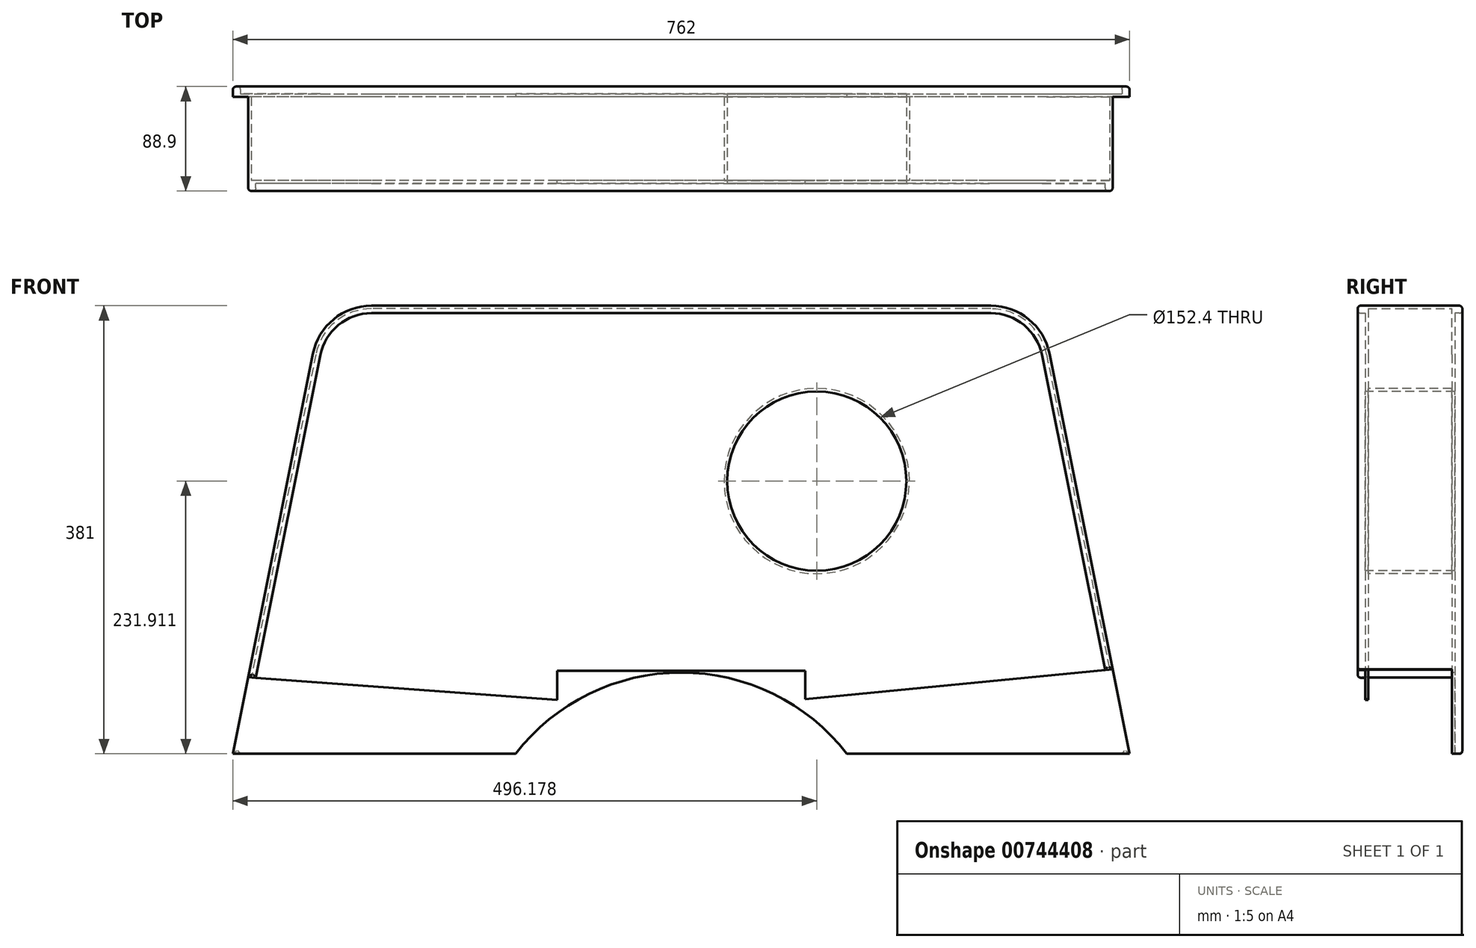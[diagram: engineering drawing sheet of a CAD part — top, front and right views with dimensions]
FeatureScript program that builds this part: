
annotation { "Feature Type Name" : "Feature", "Feature Type Description" : "" }
export const myFeature = defineFeature(function(context is Context, id is Id, definition is map)
    precondition{}
    {
        {
            var Q0;
            Q0=qCreatedBy(makeId("Top.planeOp"),FACE);
            var sketch = newSketch(context, id + "F0", { "sketchPlane" : qUnion([Q0])});
            skLineSegment(sketch, "E0.bottom", {"start": v(381, -38.1) * mm, "end": v(-381, -38.1) * mm});
            skLineSegment(sketch, "E0.top", {"start": v(381, 38.1) * mm, "end": v(-381, 38.1) * mm});
            skLineSegment(sketch, "E0.left", {"start": v(381, -38.1) * mm, "end": v(381, 38.1) * mm});
            skLineSegment(sketch, "E0.right", {"start": v(-381, -38.1) * mm, "end": v(-381, 38.1) * mm});
            skPoint(sketch, "E0.middle", {"position": v(0, 0) * mm});
            skSolve(sketch);
        }
        {
            var Q0;
            Q0=qSketchRegion(id+"F0",true);
            extrude(context, id + "F1", {"entities" : qUnion([Q0]), "depth" : 609.6 * mm});
        }
        {
            var Q0;
            Q0=makeQuery(id+"F1.opExtrude","SWEPT_FACE",FACE,{"disambiguationData":[OSD([sQuery(id+"F0.wireOp",EDGE,"E0.bottom")])]});
            var sketch = newSketch(context, id + "F2", { "sketchPlane" : qUnion([Q0])});
            skLineSegment(sketch, "E1", {"start": v(0, 381) * mm, "end": v(-304.8, 381) * mm});
            skLineSegment(sketch, "E2", {"start": v(-304.8, 381) * mm, "end": v(-381, 0) * mm});
            skLineSegment(sketch, "E3", {"start": v(0, 381) * mm, "end": v(304.8, 381) * mm});
            skLineSegment(sketch, "E4", {"start": v(304.8, 381) * mm, "end": v(381, 0) * mm});
            skPoint(sketch, "E5.center.orphan", {"position": v(0, 0) * mm});
            skSolve(sketch);
        }
        {
            var Q0;
            {var subQ1=sQuery(id+"F0.wireOp",EDGE,"E0.bottom");Q0=makeQuery(id+"F2.imprint","IMPRINT",FACE,{"disambiguationData":[TD([[makeQuery(id+"F2.imprint","IMPRINT",EDGE,{"derivedFrom":makeQuery(id+"F1.opExtrude","CAP_EDGE",EDGE,{"disambiguationData":[OSD([subQ1])],"isStart":false})}),1.0]])]});}
            extrude(context, id + "F3", {"entities" : qUnion([Q0]), "operationType" : NewBodyOperationType.REMOVE, "endBound" : BoundingType.THROUGH_ALL, "oppositeDirection" : true, "depth" : 25.4 * mm});
        }
        {
            var Q0;
            Q0=makeQuery(id+"F1.opExtrude","SWEPT_FACE",FACE,{"disambiguationData":[OSD([sQuery(id+"F0.wireOp",EDGE,"E0.bottom")])]});
            var sketch = newSketch(context, id + "F4", { "sketchPlane" : qUnion([Q0])});
            skCircle(sketch, "E6", {"center": v(115.18, 231.91) * mm, "radius": 76.2 * mm});
            skSolve(sketch);
        }
        {
            var Q0;
            Q0=makeQuery(id+"F4.imprint","IMPRINT",FACE,{"disambiguationData":[TD([[makeQuery(id+"F4.imprint","IMPRINT",EDGE,{"derivedFrom":sQuery(id+"F4.wireOp",EDGE,"E6")}),1.0]])]});
            extrude(context, id + "F5", {"entities" : qUnion([Q0]), "operationType" : NewBodyOperationType.REMOVE, "endBound" : BoundingType.THROUGH_ALL, "oppositeDirection" : true, "depth" : 25.4 * mm});
        }
        {
            var Q0;
            Q0=makeQuery(id+"F1.opExtrude","CAP_FACE",FACE,{"disambiguationData":[OSD([sQuery(id+"F0.wireOp",EDGE,"E0.bottom"),sQuery(id+"F0.wireOp",EDGE,"E0.top"),sQuery(id+"F0.wireOp",EDGE,"E0.left"),sQuery(id+"F0.wireOp",EDGE,"E0.right")])],"isStart":true});
            extrude(context, id + "F6", {"entities" : qUnion([Q0]), "operationType" : NewBodyOperationType.ADD, "depth" : 203.2 * mm});
        }
        {
            var Q0;
            {var subQ0=sQuery(id+"F0.wireOp",EDGE,"E0.top");Q0=makeQuery(id+"F6.boolean.opBoolean","MERGE",FACE,{"derivedFrom":[makeQuery(id+"F1.opExtrude","SWEPT_FACE",FACE,{"disambiguationData":[OSD([subQ0])]}),makeQuery(id+"F6.opExtrude","SWEPT_FACE",FACE,{"disambiguationData":[OSD([subQ0])]})]});}
            shell(context, id + "F7", {"entities" : qUnion([Q0]), "thickness" : 76.2 * mm});
        }
        {
            var Q0;
            {var subQ0=sQuery(id+"F0.wireOp",EDGE,"E0.top");Q0=makeQuery(id+"F6.boolean.opBoolean","MERGE",FACE,{"derivedFrom":[makeQuery(id+"F1.opExtrude","SWEPT_FACE",FACE,{"disambiguationData":[OSD([subQ0])]}),makeQuery(id+"F6.opExtrude","SWEPT_FACE",FACE,{"disambiguationData":[OSD([subQ0])]})]});}
            var sketch = newSketch(context, id + "F8", { "sketchPlane" : qUnion([Q0])});
            skLineSegment(sketch, "E7", {"start": v(381, 0) * mm, "end": v(-381, 0) * mm});
            skSolve(sketch);
        }
        {
            var Q0;
            {var subQ2=sQuery(id+"F0.wireOp",EDGE,"E0.top");Q0=makeQuery(id+"F8.imprint","IMPRINT",FACE,{"disambiguationData":[TD([[makeQuery(id+"F8.imprint","IMPRINT",EDGE,{"derivedFrom":makeQuery(id+"F7.opShell","OFFSET_EDGE",EDGE,{"disambiguationData":[OSD([subQ2])]})}),1.0]])]});}
            var Q1;
            {var subQ1=sQuery(id+"F0.wireOp",EDGE,"E0.top");Q1=makeQuery(id+"F8.imprint","IMPRINT",FACE,{"disambiguationData":[TD([[makeQuery(id+"F8.imprint","IMPRINT",EDGE,{"derivedFrom":makeQuery(id+"F6.opExtrude","CAP_EDGE",EDGE,{"disambiguationData":[OSD([subQ1])],"isStart":false})}),1.0]])]});}
            extrude(context, id + "F9", {"entities" : qUnion([Q0, Q1]), "operationType" : NewBodyOperationType.REMOVE, "endBound" : BoundingType.THROUGH_ALL, "oppositeDirection" : true, "depth" : 25.4 * mm});
        }
        {
            var Q0;
            Q0=qCreatedBy(makeId("Front.planeOp"),FACE);
            var sketch = newSketch(context, id + "F10", { "sketchPlane" : qUnion([Q0])});
            skCircle(sketch, "E8", {"center": v(0, -108.7) * mm, "radius": 177.8 * mm});
            skSolve(sketch);
        }
        {
            var Q0;
            Q0=qSketchRegion(id+"F10",true);
            extrude(context, id + "F11", {"entities" : qUnion([Q0]), "operationType" : NewBodyOperationType.REMOVE, "endBound" : BoundingType.SYMMETRIC, "oppositeDirection" : true, "depth" : 127 * mm});
        }
        {
            var Q0;
            {var subQ0=sQuery(id+"F0.wireOp",EDGE,"E0.bottom");Q0=makeQuery(id+"F6.boolean.opBoolean","MERGE",FACE,{"derivedFrom":[makeQuery(id+"F1.opExtrude","SWEPT_FACE",FACE,{"disambiguationData":[OSD([subQ0])]}),makeQuery(id+"F6.opExtrude","SWEPT_FACE",FACE,{"disambiguationData":[OSD([subQ0])]})]});}
            var sketch = newSketch(context, id + "F12", { "sketchPlane" : qUnion([Q0])});
            skLineSegment(sketch, "E9", {"start": v(-89.74, 44.8) * mm, "end": v(89.74, 44.8) * mm});
            skLineSegment(sketch, "E10", {"start": v(-89.74, 44.8) * mm, "end": v(-375.29, 65.72) * mm});
            skLineSegment(sketch, "E11", {"start": v(374.04, 72.49) * mm, "end": v(89.74, 44.8) * mm});
            skSolve(sketch);
        }
        {
            var Q0;
            {var subQ3=sQuery(id+"F0.wireOp",EDGE,"E0.bottom");var subQ4=makeQuery(id+"F6.boolean.opBoolean","MERGE",FACE,{"derivedFrom":[makeQuery(id+"F1.opExtrude","SWEPT_FACE",FACE,{"disambiguationData":[OSD([subQ3])]}),makeQuery(id+"F6.opExtrude","SWEPT_FACE",FACE,{"disambiguationData":[OSD([subQ3])]})]});var subQ7=makeQuery(id+"F11.boolean.opBoolean","SPLIT",EDGE,{"disambiguationData":[OD(1.0)],"derivedFrom":makeQuery(id+"F9.boolean.opBoolean","INTERSECT",EDGE,{"derivedFrom":[subQ4,makeQuery(id+"F9.opExtrude","SWEPT_FACE",FACE,{"disambiguationData":[OSD([sQuery(id+"F8.wireOp",EDGE,"E7")])]})]})});Q0=makeQuery(id+"F12.imprint","IMPRINT",FACE,{"disambiguationData":[TD([[makeQuery(id+"F12.imprint","IMPRINT",EDGE,{"derivedFrom":subQ7}),-1.0]])]});}
            var Q1;
            {var subQ3=sQuery(id+"F0.wireOp",EDGE,"E0.bottom");var subQ4=makeQuery(id+"F6.boolean.opBoolean","MERGE",FACE,{"derivedFrom":[makeQuery(id+"F1.opExtrude","SWEPT_FACE",FACE,{"disambiguationData":[OSD([subQ3])]}),makeQuery(id+"F6.opExtrude","SWEPT_FACE",FACE,{"disambiguationData":[OSD([subQ3])]})]});var subQ7=makeQuery(id+"F11.boolean.opBoolean","SPLIT",EDGE,{"disambiguationData":[OD(0.0)],"derivedFrom":makeQuery(id+"F9.boolean.opBoolean","INTERSECT",EDGE,{"derivedFrom":[subQ4,makeQuery(id+"F9.opExtrude","SWEPT_FACE",FACE,{"disambiguationData":[OSD([sQuery(id+"F8.wireOp",EDGE,"E7")])]})]})});Q1=makeQuery(id+"F12.imprint","IMPRINT",FACE,{"disambiguationData":[TD([[makeQuery(id+"F12.imprint","IMPRINT",EDGE,{"derivedFrom":subQ7}),-1.0]])]});}
            extrude(context, id + "F13", {"entities" : qUnion([Q0, Q1]), "operationType" : NewBodyOperationType.REMOVE, "oppositeDirection" : true, "depth" : 73.66 * mm});
        }
        {
            var Q0;
            Q0=makeQuery(id+"F3.boolean.opBoolean","COPY",EDGE,{"derivedFrom":makeQuery(id+"F3.opExtrude","SWEPT_EDGE",EDGE,{"disambiguationData":[OSD([sQuery(id+"F2.wireOp",EDGE,"E1"),sQuery(id+"F2.wireOp",EDGE,"E2")])]})});
            var Q1;
            Q1=makeQuery(id+"F3.boolean.opBoolean","COPY",EDGE,{"derivedFrom":makeQuery(id+"F3.opExtrude","SWEPT_EDGE",EDGE,{"disambiguationData":[OSD([sQuery(id+"F2.wireOp",EDGE,"E3"),sQuery(id+"F2.wireOp",EDGE,"E4")])]})});
            fillet(context, id + "F14", {"entities" : qUnion([Q0, Q1]), "radius" : 50.8 * mm, "tangentPropagation" : true, "allowEdgeOverflow" : false});
        }
        {
            var Q0;
            Q0=makeQuery(id+"F11.boolean.opBoolean","COPY",FACE,{"derivedFrom":makeQuery(id+"F11.opExtrude","SWEPT_FACE",FACE,{"disambiguationData":[OSD([sQuery(id+"F10.wireOp",EDGE,"E8")])]})});
            var Q1;
            Q1=makeQuery(id+"F13.boolean.opBoolean","COPY",FACE,{"derivedFrom":makeQuery(id+"F13.opExtrude","SWEPT_FACE",FACE,{"disambiguationData":[OSD([sQuery(id+"F12.wireOp",EDGE,"E10")])]})});
            var Q2;
            Q2=makeQuery(id+"F13.boolean.opBoolean","COPY",FACE,{"derivedFrom":makeQuery(id+"F13.opExtrude","SWEPT_FACE",FACE,{"disambiguationData":[OSD([sQuery(id+"F12.wireOp",EDGE,"E11")])]})});
            shell(context, id + "F15", {"entities" : qUnion([Q0, Q1, Q2]), "thickness" : 2.54 * mm});
        }
        {
            var Q0;
            {var subQ0=sQuery(id+"F0.wireOp",EDGE,"E0.bottom");Q0=makeQuery(id+"F6.boolean.opBoolean","MERGE",FACE,{"derivedFrom":[makeQuery(id+"F1.opExtrude","SWEPT_FACE",FACE,{"disambiguationData":[OSD([subQ0])]}),makeQuery(id+"F6.opExtrude","SWEPT_FACE",FACE,{"disambiguationData":[OSD([subQ0])]})]});}
            var sketch = newSketch(context, id + "F16", { "sketchPlane" : qUnion([Q0])});
            skLineSegment(sketch, "E12.bottom", {"start": v(105.5, 12.76) * mm, "end": v(-105.5, 12.76) * mm});
            skLineSegment(sketch, "E12.top", {"start": v(105.5, 70.56) * mm, "end": v(-105.5, 70.56) * mm});
            skLineSegment(sketch, "E12.left", {"start": v(105.5, 12.76) * mm, "end": v(105.5, 70.56) * mm});
            skLineSegment(sketch, "E12.right", {"start": v(-105.5, 12.76) * mm, "end": v(-105.5, 70.56) * mm});
            skPoint(sketch, "E12.middle", {"position": v(0, 41.66) * mm});
            skSolve(sketch);
        }
        {
            var Q0;
            Q0=qSketchRegion(id+"F16",true);
            extrude(context, id + "F17", {"entities" : qUnion([Q0]), "operationType" : NewBodyOperationType.REMOVE, "oppositeDirection" : true, "depth" : 25.4 * mm});
        }
        {
            var Q0;
            {var subQ0=sQuery(id+"F0.wireOp",EDGE,"E0.top");Q0=makeQuery(id+"F6.boolean.opBoolean","MERGE",FACE,{"derivedFrom":[makeQuery(id+"F1.opExtrude","SWEPT_FACE",FACE,{"disambiguationData":[OSD([subQ0])]}),makeQuery(id+"F6.opExtrude","SWEPT_FACE",FACE,{"disambiguationData":[OSD([subQ0])]})]});}
            var sketch = newSketch(context, id + "F18", { "sketchPlane" : qUnion([Q0])});
            skLineSegment(sketch, "E13.0", {"start": v(-306.74, 338.92) * mm, "end": v(-374.77, -1.25) * mm});
            skLineSegment(sketch, "E13.1", {"start": v(306.74, 338.92) * mm, "end": v(374.77, -1.25) * mm});
            skArc(sketch, "E13.2", {"start": v(306.74, 338.92) * mm, "mid": v(291.33, 364.58) * mm, "end": v(263.15, 374.65) * mm});
            skLineSegment(sketch, "E13.3", {"start": v(263.15, 374.65) * mm, "end": v(-263.15, 374.65) * mm});
            skArc(sketch, "E13.4", {"start": v(-263.15, 374.65) * mm, "mid": v(-291.33, 364.58) * mm, "end": v(-306.74, 338.92) * mm});
            skSolve(sketch);
        }
        {
            var Q0;
            {var subQ20=sQuery(id+"F18.wireOp",EDGE,"E13.2");Q0=makeQuery(id+"F18.imprint","IMPRINT",FACE,{"disambiguationData":[TD([[makeQuery(id+"F18.imprint","IMPRINT",EDGE,{"derivedFrom":subQ20}),-1.0]])]});}
            extrude(context, id + "F19", {"entities" : qUnion([Q0]), "operationType" : NewBodyOperationType.ADD, "depth" : 6.35 * mm});
        }
        {
            var Q0;
            {var subQ0=sQuery(id+"F0.wireOp",EDGE,"E0.bottom");Q0=makeQuery(id+"F6.boolean.opBoolean","MERGE",FACE,{"derivedFrom":[makeQuery(id+"F1.opExtrude","SWEPT_FACE",FACE,{"disambiguationData":[OSD([subQ0])]}),makeQuery(id+"F6.opExtrude","SWEPT_FACE",FACE,{"disambiguationData":[OSD([subQ0])]})]});}
            var sketch = newSketch(context, id + "F20", { "sketchPlane" : qUnion([Q0])});
            skLineSegment(sketch, "E14.0", {"start": v(-306.74, 338.92) * mm, "end": v(-361.74, 63.94) * mm});
            skLineSegment(sketch, "E14.1", {"start": v(306.74, 338.92) * mm, "end": v(360.42, 70.52) * mm});
            skArc(sketch, "E14.2", {"start": v(306.74, 338.92) * mm, "mid": v(291.33, 364.58) * mm, "end": v(263.15, 374.65) * mm});
            skLineSegment(sketch, "E14.3", {"start": v(-263.15, 374.65) * mm, "end": v(263.15, 374.65) * mm});
            skArc(sketch, "E14.4", {"start": v(-263.15, 374.65) * mm, "mid": v(-291.33, 364.58) * mm, "end": v(-306.74, 338.92) * mm});
            skSolve(sketch);
        }
        {
            var Q0;
            {var subQ12=sQuery(id+"F20.wireOp",EDGE,"E14.2");Q0=makeQuery(id+"F20.imprint","IMPRINT",FACE,{"disambiguationData":[TD([[makeQuery(id+"F20.imprint","IMPRINT",EDGE,{"derivedFrom":subQ12}),-1.0]])]});}
            extrude(context, id + "F21", {"entities" : qUnion([Q0]), "operationType" : NewBodyOperationType.ADD, "depth" : 6.35 * mm});
        }
        {
            var Q0;
            Q0=makeQuery(id+"F21.opExtrude","CAP_FACE",FACE,{"disambiguationData":[OSD([sQuery(id+"F0.wireOp",EDGE,"E0.bottom"),sQuery(id+"F2.wireOp",EDGE,"E1"),sQuery(id+"F2.wireOp",EDGE,"E2"),sQuery(id+"F2.wireOp",EDGE,"E3"),sQuery(id+"F2.wireOp",EDGE,"E4"),sQuery(id+"F12.wireOp",EDGE,"E10"),sQuery(id+"F12.wireOp",EDGE,"E11"),sQuery(id+"F20.wireOp",EDGE,"E14.0"),sQuery(id+"F20.wireOp",EDGE,"E14.1"),sQuery(id+"F20.wireOp",EDGE,"E14.2"),sQuery(id+"F20.wireOp",EDGE,"E14.3"),sQuery(id+"F20.wireOp",EDGE,"E14.4")])],"isStart":false});
            var Q1;
            Q1=makeQuery(id+"F19.opExtrude","CAP_FACE",FACE,{"disambiguationData":[OSD([sQuery(id+"F0.wireOp",EDGE,"E0.top"),sQuery(id+"F2.wireOp",EDGE,"E1"),sQuery(id+"F2.wireOp",EDGE,"E2"),sQuery(id+"F2.wireOp",EDGE,"E3"),sQuery(id+"F2.wireOp",EDGE,"E4"),sQuery(id+"F8.wireOp",EDGE,"E7"),sQuery(id+"F18.wireOp",EDGE,"E13.0"),sQuery(id+"F18.wireOp",EDGE,"E13.1"),sQuery(id+"F18.wireOp",EDGE,"E13.2"),sQuery(id+"F18.wireOp",EDGE,"E13.3"),sQuery(id+"F18.wireOp",EDGE,"E13.4")])],"isStart":false});
            fillet(context, id + "F22", {"entities" : qUnion([Q0, Q1]), "radius" : 2.54 * mm, "tangentPropagation" : true, "allowEdgeOverflow" : false});
        }
    });
